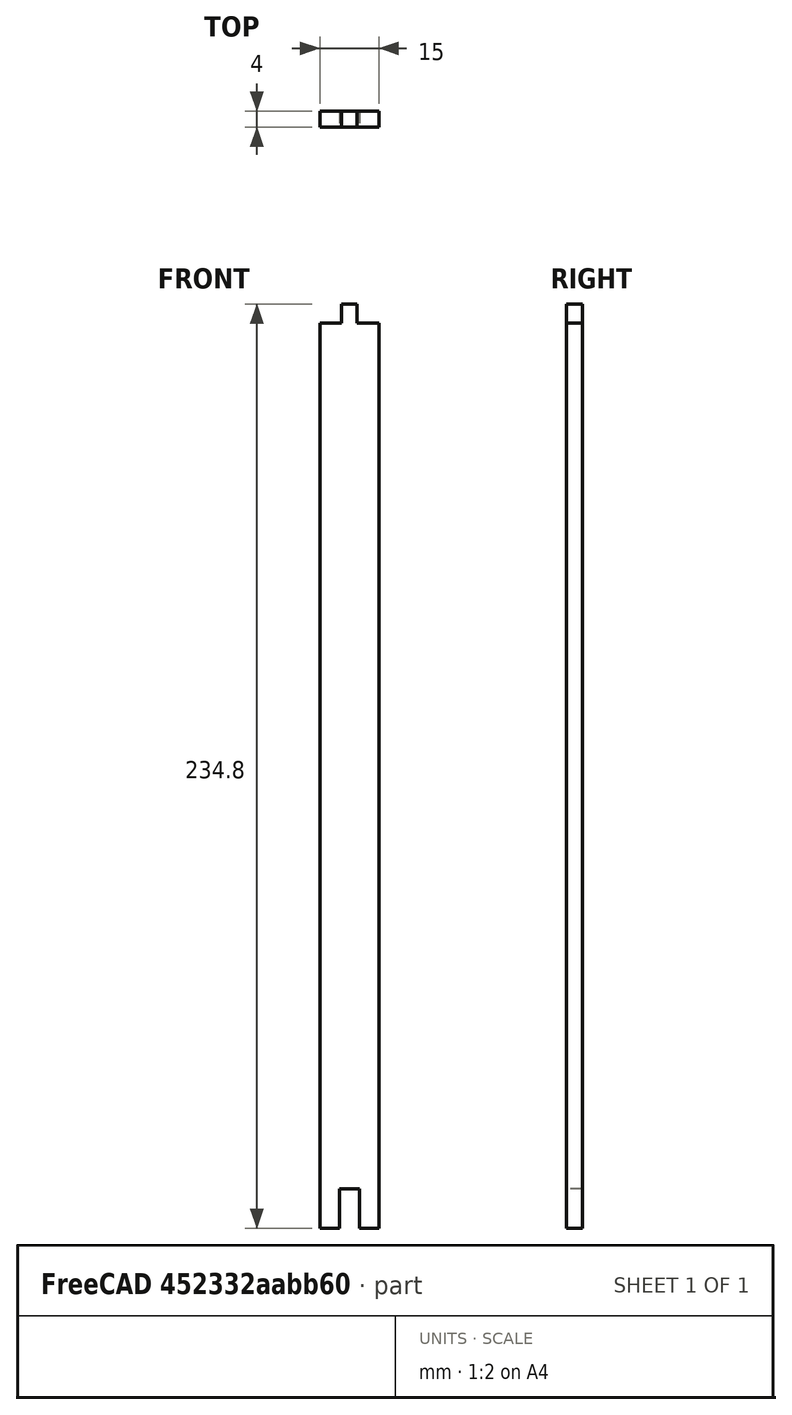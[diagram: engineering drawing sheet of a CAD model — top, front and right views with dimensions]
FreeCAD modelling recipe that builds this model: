
FCSTD DOCUMENT  (FreeCAD 1.0R39319 (Git))
Label: Base Connection Leg
License: All rights reserved
LicenseURL: https://en.wikipedia.org/wiki/All_rights_reserved
objects: PartDesign::CoordinateSystem×2, Sketcher::SketchObject×1, PartDesign::Pad×1, PartDesign::Body×1, App::Part×1
note: 8 computed .brp shape members not serialized (recipe doc carries the construction recipe); baked Part::Feature solids carry a one-line shape summary decoded from their .brp

FEATURE [Sketcher::SketchObject] Sketch
  ArcFitTolerance = 1e-06
  AttachmentSupport = -> [XZ_Plane001]
  FullyConstrained = true
  MakeInternals = false
  MapMode = 5
  Placement = pos=(0,0,0) rot=(1,0,0;1.5708rad)
  sketch-geometry (14):
    g0: LineSegment StartX=-7.5 StartY=230 StartZ=0 EndX=-7.5 EndY=0 EndZ=0
    g1: LineSegment StartX=-7.5 StartY=-4e-16 StartZ=0 EndX=-2.55 EndY=-4e-16 EndZ=0
    g2: LineSegment StartX=7.5 StartY=-9e-16 StartZ=0 EndX=7.5 EndY=230 EndZ=0
    g3: LineSegment StartX=7.5 StartY=230 StartZ=0 EndX=1.95 EndY=230 EndZ=0
    g4: LineSegment StartX=-1.95 StartY=234.8 StartZ=0 EndX=-1.95 EndY=230 EndZ=0
    g5: LineSegment StartX=1.95 StartY=230 StartZ=0 EndX=1.95 EndY=234.8 EndZ=0
    g6: LineSegment StartX=1.95 StartY=234.8 StartZ=0 EndX=-1.95 EndY=234.8 EndZ=0
    g7: LineSegment StartX=2.55 StartY=-9e-16 StartZ=0 EndX=2.55 EndY=10 EndZ=0
    g8: LineSegment StartX=2.55 StartY=10 StartZ=0 EndX=-2.55 EndY=10 EndZ=0
    g9: LineSegment StartX=-2.55 StartY=10 StartZ=0 EndX=-2.55 EndY=0 EndZ=0
    g10: LineSegment StartX=2.55 StartY=-9e-16 StartZ=0 EndX=7.5 EndY=-9e-16 EndZ=0
    g11: LineSegment StartX=-1.95 StartY=230 StartZ=0 EndX=-7.5 EndY=230 EndZ=0
    g12: GeomPoint [constr] X=0 Y=10 Z=0
    g13: GeomPoint [constr] X=3e-16 Y=234.8 Z=0
  constraints (38):
    c: Coincident(g0,g1)
    c: Coincident(g10,g2)
    c: Coincident(g2,g3)
    c: Coincident(g11,g0)
    c: Vertical(g0)
    c: Vertical(g2)
    c: Horizontal(g1)
    c: Horizontal(g3)
    c: Coincident(g5,g6)
    c: Coincident(g6,g4)
    c: Vertical(g4)
    c: Vertical(g5)
    c: Horizontal(g6)
    c: Coincident(g7,g8)
    c: Coincident(g8,g9)
    c: Horizontal(g8)
    c: Vertical(g7)
    c: Vertical(g9)
    c: Coincident(g4,g11)
    c: Coincident(g5,g3)
    c: Coincident(g9,g1)
    c: Coincident(g7,g10)
    c: PointOnObject(g1,g10)
    c: Horizontal(g10)
    c: Horizontal(g11)
    c: PointOnObject(g3,g11)
    c: DistanceX(g6,g6) = 3.9
    c: DistanceY(g5,g5) = 4.8
    c: DistanceY(g9,g9) = 10
    c: DistanceX(g8,g8) = 5.1
    c: Distance(g2,g0) = 15
    c: Symmetric(g8,g8,g12)
    c: Symmetric(g6,g6,g13)
    c: Distance(g13,g0) = 7.5
    c: Distance(g12,g0) = 7.5
    c: Distance(g11,g1) = 230
    c: PointOnObject(g12,g-2)
    c: PointOnObject(g0,g-1)
FEATURE [PartDesign::Pad] Pad
  Direction = (0,-1,2e-16)
  Length = 4
  Length2 = 10
  Midplane = true
  Placement = pos=(0,0,0) rot=(1,0,0;1.5708rad)
  Profile = -> Sketch
  ReferenceAxis = -> Sketch [N_Axis]
  Refine = true
  Suppressed = false
  Type = 0
FEATURE [PartDesign::Body] Body  label="Base Connection Leg001"
  AllowCompound = false
  Group = -> [Sketch,Pad]
  Origin = -> Origin001
  Tip = -> Pad
FEATURE [PartDesign::CoordinateSystem] LCS_1
  AttacherType = Attacher::AttachEngine3D
  AttachmentOffset = pos=(0,0,10) rot=(0,0,1;0rad)
  AttachmentSupport = -> [XY_Plane001]
  MapMode = 2
  Placement = pos=(0,0,10) rot=(0,0,1;0rad)
FEATURE [PartDesign::CoordinateSystem] LCS_2
  AttacherType = Attacher::AttachEngine3D
  AttachmentOffset = pos=(0,0,230) rot=(0,0,1;0rad)
  AttachmentSupport = -> [XY_Plane001]
  MapMode = 2
  Placement = pos=(0,0,230) rot=(0,0,1;0rad)
FEATURE [App::Part] Part  label="Base Connection Leg"
  Group = -> [Body,LCS_1,LCS_2]
  Origin = -> Origin
